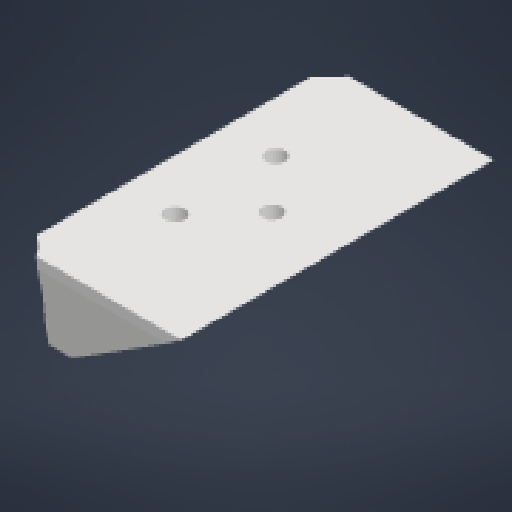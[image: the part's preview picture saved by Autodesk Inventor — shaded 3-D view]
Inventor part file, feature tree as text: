
AUTODESK INVENTOR PART (.ipt)
format: ipt  version: 2024 (Build 280153000, 153)  size: 138,752 bytes
history: native  units: in
note: dims shown in document units (in); Inventor stores cm internally (conversion verified against a paired STEP export)
features: reference x8, other x6, extrude x3, sketch x3, chamfer x2
ambient origin geometry x8: Origin, YZ Plane, XZ Plane, XY Plane, X Axis, Y Axis, Z Axis, Center Point
bodies: Solid1 (feature_tree)
feature tree (22):
  extrude  "Extrusion1"  Depth=0.2756in
  chamfer  "Chamfer1"  Distance=2.6875in
  chamfer  "Chamfer2"  Distance=0.1875in Angle=75.0deg
  extrude  "Extrusion2"  Depth=0.2165in TaperAngle=0.0deg
  extrude  "Extrusion3"  [1 undecoded]
  sketch  "Sketch1"  dims[d0=0.9963in d1=0.2756in d2=2.6875in d3=0.0in d4=0.1875in d5=0.125in d6=75.0deg]
  reference  "Reference1"
  sketch  "Sketch2"  dims[d7=0.0787in d8=0.125in d9=45.0deg d10=0.2165in d11=0.0in]
  reference  "Reference2"
  reference  "Reference3"
  reference  "Reference4"
  sketch  "Sketch3"  dims[d12=1.0in d13=0.0344in]
  reference  "Reference5"
  reference  "Reference6"
  reference  "Reference7"
  reference  "Reference8"
  other  "<userpath>\Desktop\SeniorDesign\Head_V3\Head_V3_Assembly.iam"
  other  "Head_V3_Assembly.iam"
  other  "Head_base_mount:1"
  other  "<userpath>\Desktop\SeniorDesign\Head_V3\Robot_Head_Neck_Assembly.iam"
  other  "Robot_Head_Neck_Assembly.iam"
  other  "Neck_Baseplate_V2:1"
note: 1 required parameter value undecoded (feature->parameter linkage not recoverable at this tier; creation-order binding heuristic only, values carry confidence <= 0.55)
